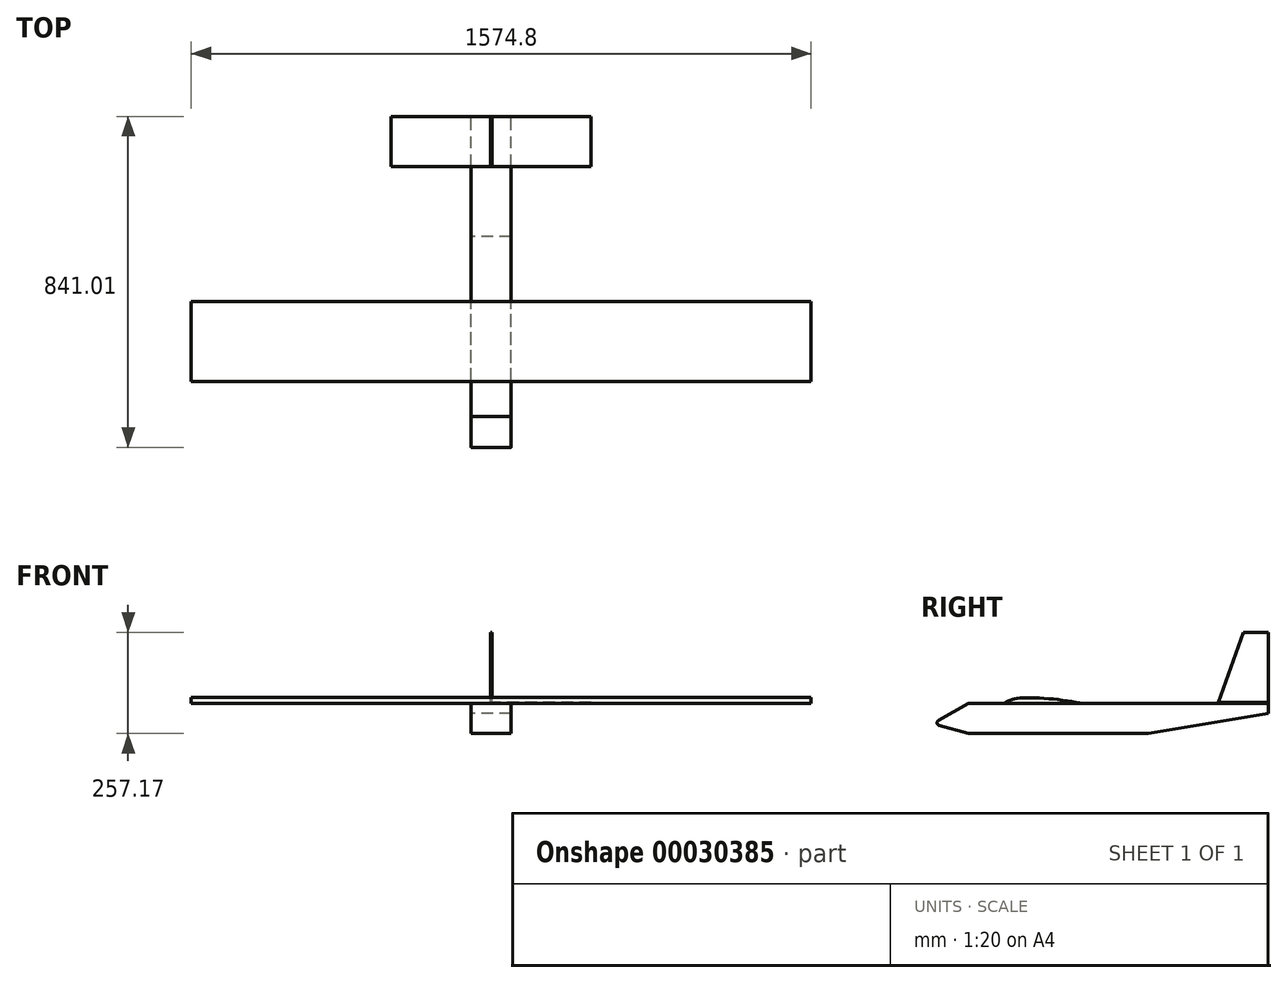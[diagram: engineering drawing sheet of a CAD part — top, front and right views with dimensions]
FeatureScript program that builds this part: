
annotation { "Feature Type Name" : "Feature", "Feature Type Description" : "" }
export const myFeature = defineFeature(function(context is Context, id is Id, definition is map)
    precondition{}
    {
        {
            var Q0;
            Q0=qCreatedBy(makeId("Right.planeOp"),FACE);
            var sketch = newSketch(context, id + "F0", { "sketchPlane" : qUnion([Q0])});
            skLineSegment(sketch, "E0", {"start": v(-381, 38.1) * mm, "end": v(381, 38.1) * mm});
            skLineSegment(sketch, "E1", {"start": v(-381, 38.1) * mm, "end": v(-381, -38.1) * mm});
            skLineSegment(sketch, "E2", {"start": v(-381, -38.1) * mm, "end": v(76.2, -38.1) * mm});
            skLineSegment(sketch, "E3", {"start": v(381, 12.7) * mm, "end": v(381, 38.1) * mm});
            skLineSegment(sketch, "E4", {"start": v(-381, 38.1) * mm, "end": v(-456.81, -5.22) * mm});
            skLineSegment(sketch, "E5", {"start": v(-455.4, -16.84) * mm, "end": v(-381, -38.1) * mm});
            skPoint(sketch, "E6.visualSharp", {"position": v(-469.9, -12.7) * mm});
            skArc(sketch, "E6.filletArc", {"start": v(-456.81, -5.22) * mm, "mid": v(-459.97, -11.5) * mm, "end": v(-455.4, -16.84) * mm});
            skLineSegment(sketch, "E7", {"start": v(381, 12.7) * mm, "end": v(76.2, -38.1) * mm});
            skPoint(sketch, "E8.orphan", {"position": v(381, -38.1) * mm});
            skSolve(sketch);
        }
        {
            var Q0;
            Q0=makeQuery(id+"F0.imprint","IMPRINT",FACE,{"disambiguationData":[TD([[makeQuery(id+"F0.imprint","IMPRINT",EDGE,{"derivedFrom":sQuery(id+"F0.wireOp",EDGE,"E0")}),-1.0]])]});
            var Q1;
            Q1=makeQuery(id+"F0.imprint","IMPRINT",FACE,{"disambiguationData":[TD([[makeQuery(id+"F0.imprint","IMPRINT",EDGE,{"derivedFrom":sQuery(id+"F0.wireOp",EDGE,"E1")}),-1.0]])]});
            extrude(context, id + "F1", {"entities" : qUnion([Q0, Q1]), "depth" : 50.8 * mm, "hasSecondDirection" : true, "secondDirectionOppositeDirection" : true, "secondDirectionDepth" : 50.8 * mm});
        }
        {
            var Q0;
            Q0=makeQuery(id+"F1.opExtrude","CAP_FACE",FACE,{"disambiguationData":[OSD([sQuery(id+"F0.wireOp",EDGE,"E0"),sQuery(id+"F0.wireOp",EDGE,"E2"),sQuery(id+"F0.wireOp",EDGE,"E3"),sQuery(id+"F0.wireOp",EDGE,"E4"),sQuery(id+"F0.wireOp",EDGE,"E5"),sQuery(id+"F0.wireOp",EDGE,"E6.filletArc"),sQuery(id+"F0.wireOp",EDGE,"E7")])],"isStart":false});
            var sketch = newSketch(context, id + "F2", { "sketchPlane" : qUnion([Q0])});
            skPoint(sketch, "E9", {"position": v(-292.1, 38.1) * mm});
            skLineSegment(sketch, "E10", {"start": v(-292.1, 38.1) * mm, "end": v(-88.9, 38.1) * mm});
            skFitSpline(sketch, "E11", {"points": [v(-292.1, 38.1) * mm, v(-249.93, 51.96) * mm, v(-88.9, 38.1) * mm], "startDerivative": vector(95.14, 47.1) * mm, "endDerivative": vector(201.66, -40.52) * mm});
            skSolve(sketch);
        }
        {
            var Q0;
            Q0=makeQuery(id+"F2.imprint","IMPRINT",FACE,{"disambiguationData":[TD([[makeQuery(id+"F2.imprint","IMPRINT",EDGE,{"derivedFrom":sQuery(id+"F2.wireOp",EDGE,"E10")}),1.0]])]});
            extrude(context, id + "F3", {"entities" : qUnion([Q0]), "operationType" : NewBodyOperationType.ADD, "depth" : 762 * mm, "hasSecondDirection" : true, "secondDirectionOppositeDirection" : true, "secondDirectionDepth" : 50.8 * mm});
        }
        {
            var Q0;
            Q0=makeQuery(id+"F3.opExtrude","CAP_FACE",FACE,{"disambiguationData":[OSD([sQuery(id+"F2.wireOp",EDGE,"E10"),sQuery(id+"F2.wireOp",EDGE,"E11")])],"isStart":true});
            extrude(context, id + "F4", {"entities" : qUnion([Q0]), "operationType" : NewBodyOperationType.ADD, "depth" : 762 * mm});
        }
        {
            var Q0;
            {var subQ0=sQuery(id+"F0.wireOp",EDGE,"E0");var subQ4=sQuery(id+"F0.wireOp",EDGE,"E3");Q0=makeQuery(id+"F4.boolean.opBoolean","SPLIT",FACE,{"disambiguationData":[TD([makeQuery(id+"F1.opExtrude","SWEPT_FACE",FACE,{"disambiguationData":[OSD([subQ4])]})])],"derivedFrom":makeQuery(id+"F1.opExtrude","SWEPT_FACE",FACE,{"disambiguationData":[OSD([subQ0])]})});}
            var sketch = newSketch(context, id + "F5", { "sketchPlane" : qUnion([Q0])});
            skLineSegment(sketch, "E12", {"start": v(0, 254) * mm, "end": v(254, 254) * mm});
            skPoint(sketch, "E12.startSnap0", {"position": v(0, 381) * mm});
            skLineSegment(sketch, "E13", {"start": v(254, 254) * mm, "end": v(254, 381) * mm});
            skLineSegment(sketch, "E14", {"start": v(254, 381) * mm, "end": v(0, 381) * mm});
            skLineSegment(sketch, "E15.MirrorCS", {"start": v(0, 254) * mm, "end": v(-254, 254) * mm});
            skLineSegment(sketch, "E16.MirrorCS", {"start": v(-254, 254) * mm, "end": v(-254, 381) * mm});
            skLineSegment(sketch, "E17.MirrorCS", {"start": v(-254, 381) * mm, "end": v(0, 381) * mm});
            skSolve(sketch);
        }
        {
            var Q0;
            Q0 = qSketchRegion(id + "F5", true);
            extrude(context, id + "F6", {"entities" : qUnion([Q0]), "operationType" : NewBodyOperationType.ADD, "depth" : 3.17 * mm});
        }
        {
            var Q0;
            Q0=qCreatedBy(makeId("Right.planeOp"),FACE);
            var sketch = newSketch(context, id + "F7", { "sketchPlane" : qUnion([Q0])});
            skLineSegment(sketch, "E18.0", {"start": v(254, 41.27) * mm, "end": v(381, 41.27) * mm});
            skLineSegment(sketch, "E19", {"start": v(254, 41.27) * mm, "end": v(317.5, 219.08) * mm});
            skLineSegment(sketch, "E20", {"start": v(317.5, 219.08) * mm, "end": v(381, 219.08) * mm});
            skLineSegment(sketch, "E21", {"start": v(381, 219.08) * mm, "end": v(381, 41.28) * mm});
            skSolve(sketch);
        }
        {
            var Q0;
            Q0 = qSketchRegion(id + "F7", true);
            extrude(context, id + "F8", {"entities" : qUnion([Q0]), "operationType" : NewBodyOperationType.ADD, "depth" : 1.59 * mm, "hasSecondDirection" : true, "secondDirectionOppositeDirection" : true, "secondDirectionDepth" : 1.59 * mm});
        }
    });
